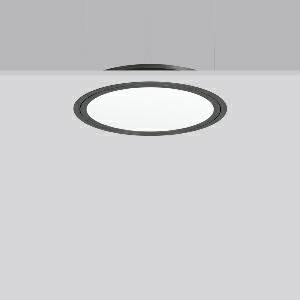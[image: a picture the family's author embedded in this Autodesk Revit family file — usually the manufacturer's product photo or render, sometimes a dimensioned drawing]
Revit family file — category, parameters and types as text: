
# Revit family: triona_round_e_312419_0031_2_12_8576
name_source: partatom
category: Lighting Fixtures
units: mm (PartAtom-declared; Revit-internal decimal feet)

## family parameters
Cut with Voids When Loaded = No
Host = Face
Light Source = No
Part Type = Normal
Room Calculation Point = No
Round Connector Dimension = Use Diameter
Shared = No

## types (1)
- TuneableWhite 846 (1 x LED Modul 846, 2450 lm, 4600)
    Apparent Load = 29 VA
    CIE Flux Codes = 48 80 96 100 100
    Color Rendering = 80
    Color Temperature = 4600
    Default Elevation = 1800 mm
    Description = Series: TRIONA round
Decorative round LED recessed surface luminaire. Cover made of sheet steel, powder-coated. Frame made of aluminium, powder-coated. Recessed ring: aluminium extrusion profile, powder coated. Light emission through a diffuser: plastic, opal. Lightguide and diffuser made of non-yellowing plastic (PMMA). Lateral light emission (RZB SIDELITE technology) for above-average homogeneous light distribution. Tunable white versions, dynamically adjustable from 2700 K to 6500 K. Suitable for installation in cavity ceilings. Tool-free mounting system thanks to the rocker arm mechanism (patent pending). Electronic ballast included. Very easy installation thanks to Plug+Play connection. Ideal for use as part of the Human Centric Lighting concept in connection with RZB light management systems. 
Colour: anthracite metallic (DB703)
Diameter: 505 mm
Height: 2 mm
Cut-out diameter: 482 mm
Recess height: 100 mm
Luminaire: recess height: 89 mm
Lamp: LED
Socket: without socket
Colour temperature: 2700K - 6500K
Colour rendering index (CRI): 80
System power: 29 W
Rated luminous flux: 2450 lm
Luminous efficiency: 84 lm/W
System power 2: 29 W
Rated luminous flux 2: 2350 lm
Luminous efficiency 2: 81 lm/W
System power 3: 30 W
Rated luminous flux 3: 2400 lm
Luminous efficiency 3: 80 lm/W
Control gear: Converter, dimmable, DALI
Protection class: I
Type of protection: IP 40
    Height = 0 mm  [stored 0 ft]
    Lamp = 1 x LED Modul 846
    Lamp Light Flux = 2450 lm
    Lamp count = 1
    Length = 505 mm
    Lifetime = 50000 h
    Luminous efficacy = 84 lm/W
    Manufacturer = RZB
    ModVariant = No
    Model = 312419.0031.2.12
    Mounting Place = Ceiling
    Mounting Type = Recessed
    Number of Poles = 1
    OnlyDefault = Yes
    Power Factor = 1
    Product Name = TRIONA round E
    Product group = Recessed modular luminaires
    ProductGroupID = 406
    Protection Class = Protection class I
    Protection Degree = IP 20
    RLX_Detail_Level = 1
    RLX_Emergency_Light_Flux = 0 lm
    RLX_Emergency_Type = 0
    RLX_Emergency_Type_DB = No
    RlxData = <blob elided: 34577 chars, md5=d01170c7>
    Socket = socket
    Standby Power = 0 W
    System Light Flux = 2450 lm
    System Power = 29 W
    Type Comments = TuneableWhite 846
    Type Image = 312419.0031.12.jpg
    URL = http://relux.com
    VarID = tuneablewhite_846
    Voltage = 230 V
    Voltage Range = 220-240 V
    Weight = 0.00 kg
    Width = 0 mm  [stored 0 ft]

note: [stored X ft] marks values corroborated as IEEE doubles in the binary element streams (Revit-internal decimal feet)

## geometry (parser evidence)
native form markers: Blend x4, Sweep x10
no freeform markers — native parametric forms only
